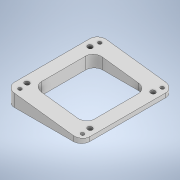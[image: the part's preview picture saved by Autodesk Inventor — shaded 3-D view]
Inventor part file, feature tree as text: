
AUTODESK INVENTOR PART (.ipt)
format: ipt  version: 2021 (Build 250183000, 183)  size: 182,272 bytes
history: native  units: mm
features: sketch x7, extrude x3, hole x3, other x2, projected_geometry x2, plane x1, fillet x1
ambient origin geometry x8: Origin, YZ Plane, XZ Plane, XY Plane, X Axis, Y Axis, Z Axis, Center Point
bodies: Body1 (feature_tree)
feature tree (19):
  other  "實體1"
  extrude  "擠出1"  Depth=180.0mm
  extrude  "擠出2"  Depth=220.0mm
  sketch  "草圖4"
  plane  "工作平面2"
  other  "分割1"
  hole  "孔1"  [1 undecoded]
  hole  "孔2"  [1 undecoded]
  hole  "孔3"  [1 undecoded]
  extrude  "擠出3"  Depth=1.22173mm
  fillet  "圓角2"  Radius=150.0mm
  sketch  "草圖1"
  sketch  "草圖3"
  projected_geometry  "投影迴路2"
  projected_geometry  "投影迴路3"
  sketch  "草圖5"
  sketch  "草圖6"
  sketch  "草圖7"
  sketch  "草圖8"
note: 3 required parameter values undecoded (feature->parameter linkage not recoverable at this tier; creation-order binding heuristic only, values carry confidence <= 0.55)
